# Revit family: Pnuematic_Valve-Acorn-04-M
name_source: partatom
category: Mechanical Equipment
units: mm (PartAtom-declared; Revit-internal decimal feet)

## family parameters
Classification = None
Cut with Voids When Loaded = No
Host = Face
OmniClass Number = 23.75.65.14.14.11
OmniClass Title = Temperature Controls
Part Type = Normal
Room Calculation Point = No
Round Connector Dimension = Use Diameter
Shared = Yes

## types (1)
- -04-M
    -BRS Brass Valve Body = No
    ADA Compliant = Yes
    Assembly Code = D2090900
    CW Connection = Yes
    CWFU = 0
    Default Elevation = 0"
    Description = Option: Master-Trol® Plus Hot & Cold Valve
    Finish = Metal-Acorn-Brass
    HW Connection = Yes
    HWFU = 0
    IAPMO Compliance = Valve conforms with the leadfree requirements of NSF61, Section 9, 1997; Federal Public Law 111-380 and ADA requirements.
    Inlet Diameter Connection = 1/2"
    Installation Type = Surface Mounted
    Manufacturer = Acorn
    Material = Metal-Acorn-Brass
    Maximum Temperature = 130º F / 54º C
    Model = -04-M
    Operating Pressure = Min/Max - 30/100 PSI
    Price = Prices may vary. Please consult Manufacturer Representative for most up-to-date price list.
    Product Documentation Link = https://www.acorneng.com
    Product Page URL = https://www.acorneng.com
    URL = https://www.acorneng.com
    Vent Connection = No
    WFU = 0
    Waste Connection = No

## geometry (parser evidence)
native form markers: Sweep x3
no freeform markers — native parametric forms only
